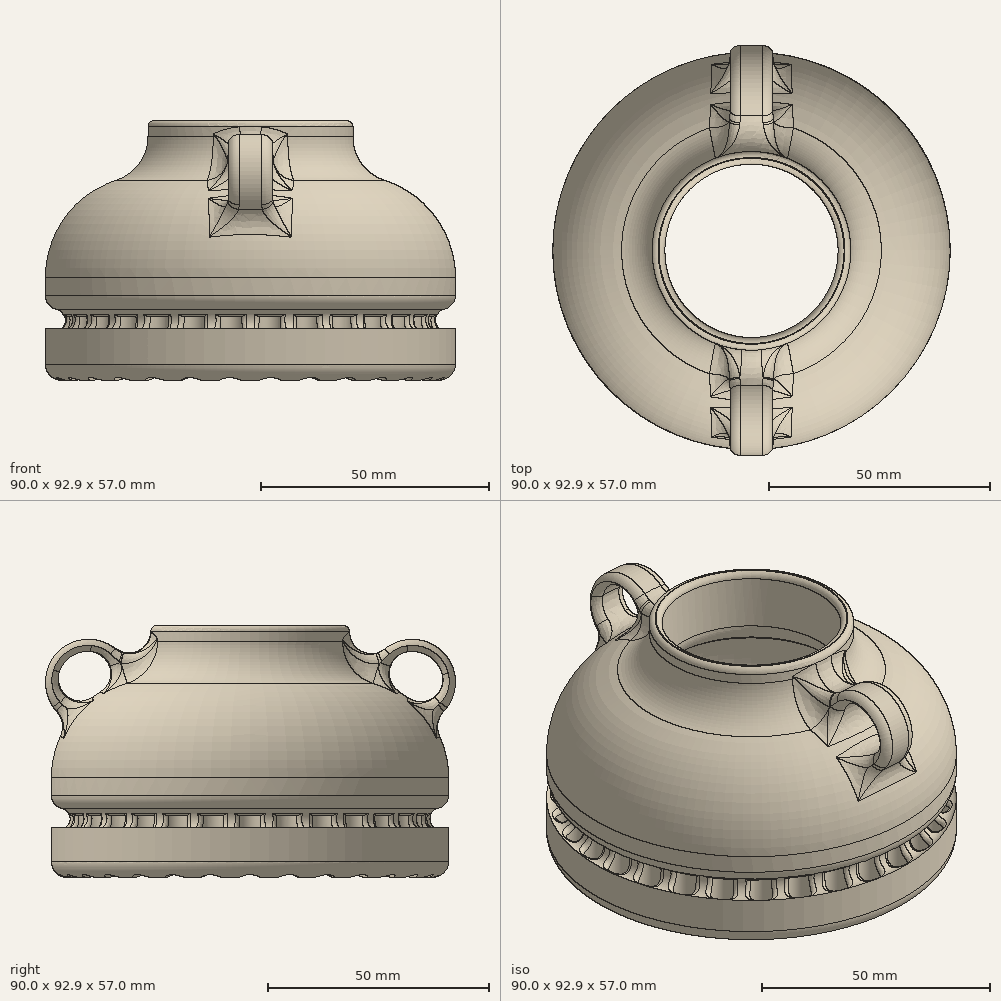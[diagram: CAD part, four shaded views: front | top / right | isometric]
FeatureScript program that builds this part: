
annotation { "Feature Type Name" : "Feature", "Feature Type Description" : "" }
export const myFeature = defineFeature(function(context is Context, id is Id, definition is map)
    precondition{}
    {
        {
            var Q0;
            Q0=qCreatedBy(makeId("Top.planeOp"),FACE);
            var sketch = newSketch(context, id + "F0", { "sketchPlane" : qUnion([Q0])});
            skCircle(sketch, "E0", {"center": v(0, 0) * mm, "radius": 45 * mm});
            skSolve(sketch);
        }
        {
            var Q0;
            Q0 = qSketchRegion(id + "F0", true);
            extrude(context, id + "F1", {"entities" : qUnion([Q0]), "depth" : 45 * mm});
        }
        {
            var Q0;
            Q0=makeQuery(id+"F1.opExtrude","CAP_EDGE",EDGE,{"disambiguationData":[OSD([sQuery(id+"F0.wireOp",EDGE,"E0")])],"isStart":false});
            fillet(context, id + "F2", {"entities" : qUnion([Q0]), "radius" : 22.5 * mm, "tangentPropagation" : true, "allowEdgeOverflow" : false});
        }
        {
            var Q0;
            Q0=makeQuery(id+"F1.opExtrude","CAP_FACE",FACE,{"disambiguationData":[OSD([sQuery(id+"F0.wireOp",EDGE,"E0")])],"isStart":false});
            var sketch = newSketch(context, id + "F3", { "sketchPlane" : qUnion([Q0])});
            skCircle(sketch, "E1", {"center": v(0, 0) * mm, "radius": 22.5 * mm});
            skSolve(sketch);
        }
        {
            var Q0;
            Q0 = qSketchRegion(id + "F3", true);
            extrude(context, id + "F4", {"entities" : qUnion([Q0]), "operationType" : NewBodyOperationType.ADD, "depth" : 12 * mm});
        }
        {
            var Q0;
            Q0=qCreatedBy(makeId("Top.planeOp"),FACE);
            var sketch = newSketch(context, id + "F5", { "sketchPlane" : qUnion([Q0])});
            skCircle(sketch, "E2", {"center": v(0, 0) * mm, "radius": 19.62 * mm});
            skSolve(sketch);
        }
        {
            var Q0;
            {var subQ0=sQuery(id+"F0.wireOp",EDGE,"E0");Q0=makeQuery(id+"F4.boolean.opBoolean","MERGE",EDGE,{"derivedFrom":[makeQuery(id+"F2.opFillet","BLEND_EDGE",EDGE,{"blendedFrom":[makeQuery(id+"F1.opExtrude","CAP_EDGE",EDGE,{"disambiguationData":[OSD([subQ0])],"isStart":false}),makeQuery(id+"F1.opExtrude","CAP_FACE",FACE,{"disambiguationData":[OSD([subQ0])],"isStart":false})],"blendedInto":[makeQuery(id+"F1.opExtrude","CAP_FACE",FACE,{"disambiguationData":[OSD([subQ0])],"isStart":false})]}),makeQuery(id+"F4.opExtrude","CAP_EDGE",EDGE,{"disambiguationData":[OSD([sQuery(id+"F3.wireOp",EDGE,"E1")])],"isStart":true})]});}
            fillet(context, id + "F6", {"entities" : qUnion([Q0]), "radius" : 10 * mm, "tangentPropagation" : true, "allowEdgeOverflow" : false});
        }
        {
            var Q0;
            Q0=makeQuery(id+"F1.opExtrude","CAP_FACE",FACE,{"disambiguationData":[OSD([sQuery(id+"F0.wireOp",EDGE,"E0")])],"isStart":true});
            shell(context, id + "F7", {"entities" : qUnion([Q0]), "thickness" : 7.5 * mm});
        }
        {
            var Q0;
            Q0 = qSketchRegion(id + "F5", true);
            extrude(context, id + "F8", {"entities" : qUnion([Q0]), "operationType" : NewBodyOperationType.REMOVE, "depth" : 80 * mm});
        }
        {
            var Q0;
            Q0=makeQuery(id+"F8.boolean.opBoolean","INTERSECT",EDGE,{"derivedFrom":[makeQuery(id+"F7.opShell","OFFSET_FACE",FACE,{"disambiguationData":[OSD([sQuery(id+"F0.wireOp",EDGE,"E0"),sQuery(id+"F3.wireOp",EDGE,"E1")])]}),makeQuery(id+"F8.opExtrude","SWEPT_FACE",FACE,{"disambiguationData":[OSD([sQuery(id+"F5.wireOp",EDGE,"E2")])]})]});
            fillet(context, id + "F9", {"entities" : qUnion([Q0]), "radius" : 5 * mm, "tangentPropagation" : true, "allowEdgeOverflow" : false});
        }
        {
            var Q0;
            Q0=makeQuery(id+"F1.opExtrude","CAP_FACE",FACE,{"disambiguationData":[OSD([sQuery(id+"F0.wireOp",EDGE,"E0")])],"isStart":true});
            var sketch = newSketch(context, id + "F10", { "sketchPlane" : qUnion([Q0])});
            skCircle(sketch, "E3", {"center": v(-40.97, 0) * mm, "radius": 2.5 * mm});
            skPoint(sketch, "E4", {"position": v(0, 0) * mm});
            skCircle(sketch, "E5.1.0", {"center": v(-40.07, -8.52) * mm, "radius": 2.5 * mm});
            skCircle(sketch, "E5.2.0", {"center": v(-37.42, -16.66) * mm, "radius": 2.5 * mm});
            skCircle(sketch, "E5.3.0", {"center": v(-33.14, -24.08) * mm, "radius": 2.5 * mm});
            skCircle(sketch, "E5.4.0", {"center": v(-27.41, -30.44) * mm, "radius": 2.5 * mm});
            skCircle(sketch, "E5.5.0", {"center": v(-20.48, -35.48) * mm, "radius": 2.5 * mm});
            skCircle(sketch, "E5.6.0", {"center": v(-12.66, -38.96) * mm, "radius": 2.5 * mm});
            skCircle(sketch, "E5.7.0", {"center": v(-4.28, -40.74) * mm, "radius": 2.5 * mm});
            skCircle(sketch, "E5.8.0", {"center": v(4.28, -40.74) * mm, "radius": 2.5 * mm});
            skCircle(sketch, "E5.9.0", {"center": v(12.66, -38.96) * mm, "radius": 2.5 * mm});
            skCircle(sketch, "E5.10.0", {"center": v(20.48, -35.48) * mm, "radius": 2.5 * mm});
            skCircle(sketch, "E5.11.0", {"center": v(27.41, -30.44) * mm, "radius": 2.5 * mm});
            skCircle(sketch, "E5.12.0", {"center": v(33.14, -24.08) * mm, "radius": 2.5 * mm});
            skCircle(sketch, "E5.13.0", {"center": v(37.42, -16.66) * mm, "radius": 2.5 * mm});
            skCircle(sketch, "E5.14.0", {"center": v(40.07, -8.52) * mm, "radius": 2.5 * mm});
            skCircle(sketch, "E5.15.0", {"center": v(40.97, 0) * mm, "radius": 2.5 * mm});
            skCircle(sketch, "E5.16.0", {"center": v(40.07, 8.52) * mm, "radius": 2.5 * mm});
            skCircle(sketch, "E5.17.0", {"center": v(37.42, 16.66) * mm, "radius": 2.5 * mm});
            skCircle(sketch, "E5.18.0", {"center": v(33.14, 24.08) * mm, "radius": 2.5 * mm});
            skCircle(sketch, "E5.19.0", {"center": v(27.41, 30.44) * mm, "radius": 2.5 * mm});
            skCircle(sketch, "E5.20.0", {"center": v(20.48, 35.48) * mm, "radius": 2.5 * mm});
            skCircle(sketch, "E5.21.0", {"center": v(12.66, 38.96) * mm, "radius": 2.5 * mm});
            skCircle(sketch, "E5.22.0", {"center": v(4.28, 40.74) * mm, "radius": 2.5 * mm});
            skCircle(sketch, "E5.23.0", {"center": v(-4.28, 40.74) * mm, "radius": 2.5 * mm});
            skCircle(sketch, "E5.24.0", {"center": v(-12.66, 38.96) * mm, "radius": 2.5 * mm});
            skCircle(sketch, "E5.25.0", {"center": v(-20.48, 35.48) * mm, "radius": 2.5 * mm});
            skCircle(sketch, "E5.26.0", {"center": v(-27.41, 30.44) * mm, "radius": 2.5 * mm});
            skCircle(sketch, "E5.27.0", {"center": v(-33.14, 24.08) * mm, "radius": 2.5 * mm});
            skCircle(sketch, "E5.28.0", {"center": v(-37.42, 16.66) * mm, "radius": 2.5 * mm});
            skCircle(sketch, "E5.29.0", {"center": v(-40.07, 8.52) * mm, "radius": 2.5 * mm});
            skSolve(sketch);
        }
        {
            var Q0;
            Q0 = qSketchRegion(id + "F10", true);
            extrude(context, id + "F11", {"entities" : qUnion([Q0]), "operationType" : NewBodyOperationType.REMOVE, "oppositeDirection" : true, "depth" : 14 * mm});
        }
        {
            var Q0;
            Q0=qCreatedBy(makeId("Front.planeOp"),FACE);
            var sketch = newSketch(context, id + "F12", { "sketchPlane" : qUnion([Q0])});
            skCircle(sketch, "E6", {"center": v(-43.26, 13.19) * mm, "radius": 2.5 * mm});
            skLineSegment(sketch, "E7", {"start": v(0, 0) * mm, "end": v(0, 30.84) * mm});
            skSolve(sketch);
        }
        {
            var Q0;
            Q0=makeQuery(id+"F12.imprint","IMPRINT",FACE,{"disambiguationData":[TD([[makeQuery(id+"F12.imprint","IMPRINT",EDGE,{"derivedFrom":sQuery(id+"F12.wireOp",EDGE,"E6")}),1.0]])]});
            var Q1;
            Q1=sQuery(id+"F12.wireOp",EDGE,"E7");
            revolve(context, id + "F13", {"operationType" : NewBodyOperationType.REMOVE, "entities" : qUnion([Q0]), "axis" : qUnion([Q1]), "revolveType" : RevolveType.FULL, "oppositeDirection" : true});
        }
        {
            var Q0;
            Q0=makeQuery(id+"F13.boolean.opBoolean","INTERSECT",EDGE,{"disambiguationData":[OD(1.0)],"derivedFrom":[makeQuery(id+"F1.opExtrude","SWEPT_FACE",FACE,{"disambiguationData":[OSD([sQuery(id+"F0.wireOp",EDGE,"E0")])]}),makeQuery(id+"F13.opRevolve","SWEPT_FACE",FACE,{"disambiguationData":[OSD([sQuery(id+"F12.wireOp",EDGE,"E6")])]})]});
            fillet(context, id + "F14", {"entities" : qUnion([Q0]), "radius" : 3 * mm, "tangentPropagation" : true, "allowEdgeOverflow" : false});
        }
        {
            var Q0;
            Q0=makeQuery(id+"F4.opExtrude","CAP_EDGE",EDGE,{"disambiguationData":[OSD([sQuery(id+"F3.wireOp",EDGE,"E1")])],"isStart":false});
            var Q1;
            Q1=makeQuery(id+"F8.boolean.opBoolean","INTERSECT",EDGE,{"derivedFrom":[makeQuery(id+"F4.opExtrude","CAP_FACE",FACE,{"disambiguationData":[OSD([sQuery(id+"F3.wireOp",EDGE,"E1")])],"isStart":false}),makeQuery(id+"F8.opExtrude","SWEPT_FACE",FACE,{"disambiguationData":[OSD([sQuery(id+"F5.wireOp",EDGE,"E2")])]})]});
            fillet(context, id + "F15", {"entities" : qUnion([Q0, Q1]), "radius" : 1.35 * mm, "tangentPropagation" : true, "allowEdgeOverflow" : false});
        }
        {
            var Q0;
            Q0=makeQuery(id+"F1.opExtrude","CAP_EDGE",EDGE,{"disambiguationData":[OSD([sQuery(id+"F0.wireOp",EDGE,"E0")])],"isStart":true});
            var Q1;
            {var subQ0=sQuery(id+"F0.wireOp",EDGE,"E0");Q1=makeQuery(id+"F7.opShell","OFFSET_EDGE",EDGE,{"disambiguationData":[OSD([subQ0]),TDD([makeQuery(id+"F1.opExtrude","CAP_EDGE",EDGE,{"disambiguationData":[OSD([subQ0])],"isStart":true})])]});}
            fillet(context, id + "F16", {"entities" : qUnion([Q0, Q1]), "radius" : 3.5 * mm, "tangentPropagation" : true, "allowEdgeOverflow" : false});
        }
        {
            var Q0;
            Q0=makeQuery(id+"F13.boolean.opBoolean","INTERSECT",EDGE,{"derivedFrom":[makeQuery(id+"F11.boolean.opBoolean","COPY",FACE,{"derivedFrom":makeQuery(id+"F11.opExtrude","SWEPT_FACE",FACE,{"disambiguationData":[OSD([sQuery(id+"F10.wireOp",EDGE,"E5.25.0")])]})}),makeQuery(id+"F13.opRevolve","SWEPT_FACE",FACE,{"disambiguationData":[OSD([sQuery(id+"F12.wireOp",EDGE,"E6")])]})]});
            var Q1;
            Q1=makeQuery(id+"F13.boolean.opBoolean","INTERSECT",EDGE,{"derivedFrom":[makeQuery(id+"F11.boolean.opBoolean","COPY",FACE,{"derivedFrom":makeQuery(id+"F11.opExtrude","CAP_FACE",FACE,{"disambiguationData":[OSD([sQuery(id+"F10.wireOp",EDGE,"E5.25.0")])],"isStart":false})}),makeQuery(id+"F13.opRevolve","SWEPT_FACE",FACE,{"disambiguationData":[OSD([sQuery(id+"F12.wireOp",EDGE,"E6")])]})]});
            var Q2;
            Q2=makeQuery(id+"F13.boolean.opBoolean","INTERSECT",EDGE,{"derivedFrom":[makeQuery(id+"F11.boolean.opBoolean","COPY",FACE,{"derivedFrom":makeQuery(id+"F11.opExtrude","SWEPT_FACE",FACE,{"disambiguationData":[OSD([sQuery(id+"F10.wireOp",EDGE,"E5.26.0")])]})}),makeQuery(id+"F13.opRevolve","SWEPT_FACE",FACE,{"disambiguationData":[OSD([sQuery(id+"F12.wireOp",EDGE,"E6")])]})]});
            var Q3;
            Q3=makeQuery(id+"F13.boolean.opBoolean","INTERSECT",EDGE,{"derivedFrom":[makeQuery(id+"F11.boolean.opBoolean","COPY",FACE,{"derivedFrom":makeQuery(id+"F11.opExtrude","CAP_FACE",FACE,{"disambiguationData":[OSD([sQuery(id+"F10.wireOp",EDGE,"E5.26.0")])],"isStart":false})}),makeQuery(id+"F13.opRevolve","SWEPT_FACE",FACE,{"disambiguationData":[OSD([sQuery(id+"F12.wireOp",EDGE,"E6")])]})]});
            var Q4;
            Q4=makeQuery(id+"F13.boolean.opBoolean","INTERSECT",EDGE,{"derivedFrom":[makeQuery(id+"F11.boolean.opBoolean","COPY",FACE,{"derivedFrom":makeQuery(id+"F11.opExtrude","SWEPT_FACE",FACE,{"disambiguationData":[OSD([sQuery(id+"F10.wireOp",EDGE,"E5.27.0")])]})}),makeQuery(id+"F13.opRevolve","SWEPT_FACE",FACE,{"disambiguationData":[OSD([sQuery(id+"F12.wireOp",EDGE,"E6")])]})]});
            var Q5;
            Q5=makeQuery(id+"F13.boolean.opBoolean","INTERSECT",EDGE,{"derivedFrom":[makeQuery(id+"F11.boolean.opBoolean","COPY",FACE,{"derivedFrom":makeQuery(id+"F11.opExtrude","CAP_FACE",FACE,{"disambiguationData":[OSD([sQuery(id+"F10.wireOp",EDGE,"E5.27.0")])],"isStart":false})}),makeQuery(id+"F13.opRevolve","SWEPT_FACE",FACE,{"disambiguationData":[OSD([sQuery(id+"F12.wireOp",EDGE,"E6")])]})]});
            var Q6;
            Q6=makeQuery(id+"F13.boolean.opBoolean","INTERSECT",EDGE,{"derivedFrom":[makeQuery(id+"F11.boolean.opBoolean","COPY",FACE,{"derivedFrom":makeQuery(id+"F11.opExtrude","SWEPT_FACE",FACE,{"disambiguationData":[OSD([sQuery(id+"F10.wireOp",EDGE,"E5.28.0")])]})}),makeQuery(id+"F13.opRevolve","SWEPT_FACE",FACE,{"disambiguationData":[OSD([sQuery(id+"F12.wireOp",EDGE,"E6")])]})]});
            var Q7;
            Q7=makeQuery(id+"F13.boolean.opBoolean","INTERSECT",EDGE,{"derivedFrom":[makeQuery(id+"F11.boolean.opBoolean","COPY",FACE,{"derivedFrom":makeQuery(id+"F11.opExtrude","CAP_FACE",FACE,{"disambiguationData":[OSD([sQuery(id+"F10.wireOp",EDGE,"E5.28.0")])],"isStart":false})}),makeQuery(id+"F13.opRevolve","SWEPT_FACE",FACE,{"disambiguationData":[OSD([sQuery(id+"F12.wireOp",EDGE,"E6")])]})]});
            var Q8;
            Q8=makeQuery(id+"F13.boolean.opBoolean","INTERSECT",EDGE,{"derivedFrom":[makeQuery(id+"F11.boolean.opBoolean","COPY",FACE,{"derivedFrom":makeQuery(id+"F11.opExtrude","SWEPT_FACE",FACE,{"disambiguationData":[OSD([sQuery(id+"F10.wireOp",EDGE,"E5.24.0")])]})}),makeQuery(id+"F13.opRevolve","SWEPT_FACE",FACE,{"disambiguationData":[OSD([sQuery(id+"F12.wireOp",EDGE,"E6")])]})]});
            var Q9;
            Q9=makeQuery(id+"F13.boolean.opBoolean","INTERSECT",EDGE,{"derivedFrom":[makeQuery(id+"F11.boolean.opBoolean","COPY",FACE,{"derivedFrom":makeQuery(id+"F11.opExtrude","CAP_FACE",FACE,{"disambiguationData":[OSD([sQuery(id+"F10.wireOp",EDGE,"E5.24.0")])],"isStart":false})}),makeQuery(id+"F13.opRevolve","SWEPT_FACE",FACE,{"disambiguationData":[OSD([sQuery(id+"F12.wireOp",EDGE,"E6")])]})]});
            var Q10;
            Q10=makeQuery(id+"F13.boolean.opBoolean","INTERSECT",EDGE,{"derivedFrom":[makeQuery(id+"F11.boolean.opBoolean","COPY",FACE,{"derivedFrom":makeQuery(id+"F11.opExtrude","SWEPT_FACE",FACE,{"disambiguationData":[OSD([sQuery(id+"F10.wireOp",EDGE,"E5.29.0")])]})}),makeQuery(id+"F13.opRevolve","SWEPT_FACE",FACE,{"disambiguationData":[OSD([sQuery(id+"F12.wireOp",EDGE,"E6")])]})]});
            var Q11;
            Q11=makeQuery(id+"F13.boolean.opBoolean","INTERSECT",EDGE,{"derivedFrom":[makeQuery(id+"F11.boolean.opBoolean","COPY",FACE,{"derivedFrom":makeQuery(id+"F11.opExtrude","CAP_FACE",FACE,{"disambiguationData":[OSD([sQuery(id+"F10.wireOp",EDGE,"E5.29.0")])],"isStart":false})}),makeQuery(id+"F13.opRevolve","SWEPT_FACE",FACE,{"disambiguationData":[OSD([sQuery(id+"F12.wireOp",EDGE,"E6")])]})]});
            var Q12;
            Q12=makeQuery(id+"F13.boolean.opBoolean","INTERSECT",EDGE,{"derivedFrom":[makeQuery(id+"F11.boolean.opBoolean","COPY",FACE,{"derivedFrom":makeQuery(id+"F11.opExtrude","CAP_FACE",FACE,{"disambiguationData":[OSD([sQuery(id+"F10.wireOp",EDGE,"E5.8.0")])],"isStart":false})}),makeQuery(id+"F13.opRevolve","SWEPT_FACE",FACE,{"disambiguationData":[OSD([sQuery(id+"F12.wireOp",EDGE,"E6")])]})]});
            var Q13;
            Q13=makeQuery(id+"F13.boolean.opBoolean","INTERSECT",EDGE,{"derivedFrom":[makeQuery(id+"F11.boolean.opBoolean","COPY",FACE,{"derivedFrom":makeQuery(id+"F11.opExtrude","SWEPT_FACE",FACE,{"disambiguationData":[OSD([sQuery(id+"F10.wireOp",EDGE,"E5.8.0")])]})}),makeQuery(id+"F13.opRevolve","SWEPT_FACE",FACE,{"disambiguationData":[OSD([sQuery(id+"F12.wireOp",EDGE,"E6")])]})]});
            var Q14;
            Q14=makeQuery(id+"F13.boolean.opBoolean","INTERSECT",EDGE,{"derivedFrom":[makeQuery(id+"F11.boolean.opBoolean","COPY",FACE,{"derivedFrom":makeQuery(id+"F11.opExtrude","CAP_FACE",FACE,{"disambiguationData":[OSD([sQuery(id+"F10.wireOp",EDGE,"E5.9.0")])],"isStart":false})}),makeQuery(id+"F13.opRevolve","SWEPT_FACE",FACE,{"disambiguationData":[OSD([sQuery(id+"F12.wireOp",EDGE,"E6")])]})]});
            var Q15;
            Q15=makeQuery(id+"F13.boolean.opBoolean","INTERSECT",EDGE,{"derivedFrom":[makeQuery(id+"F11.boolean.opBoolean","COPY",FACE,{"derivedFrom":makeQuery(id+"F11.opExtrude","SWEPT_FACE",FACE,{"disambiguationData":[OSD([sQuery(id+"F10.wireOp",EDGE,"E5.9.0")])]})}),makeQuery(id+"F13.opRevolve","SWEPT_FACE",FACE,{"disambiguationData":[OSD([sQuery(id+"F12.wireOp",EDGE,"E6")])]})]});
            var Q16;
            Q16=makeQuery(id+"F13.boolean.opBoolean","INTERSECT",EDGE,{"derivedFrom":[makeQuery(id+"F11.boolean.opBoolean","COPY",FACE,{"derivedFrom":makeQuery(id+"F11.opExtrude","CAP_FACE",FACE,{"disambiguationData":[OSD([sQuery(id+"F10.wireOp",EDGE,"E5.10.0")])],"isStart":false})}),makeQuery(id+"F13.opRevolve","SWEPT_FACE",FACE,{"disambiguationData":[OSD([sQuery(id+"F12.wireOp",EDGE,"E6")])]})]});
            var Q17;
            Q17=makeQuery(id+"F13.boolean.opBoolean","INTERSECT",EDGE,{"derivedFrom":[makeQuery(id+"F11.boolean.opBoolean","COPY",FACE,{"derivedFrom":makeQuery(id+"F11.opExtrude","SWEPT_FACE",FACE,{"disambiguationData":[OSD([sQuery(id+"F10.wireOp",EDGE,"E5.10.0")])]})}),makeQuery(id+"F13.opRevolve","SWEPT_FACE",FACE,{"disambiguationData":[OSD([sQuery(id+"F12.wireOp",EDGE,"E6")])]})]});
            var Q18;
            Q18=makeQuery(id+"F13.boolean.opBoolean","INTERSECT",EDGE,{"derivedFrom":[makeQuery(id+"F11.boolean.opBoolean","COPY",FACE,{"derivedFrom":makeQuery(id+"F11.opExtrude","CAP_FACE",FACE,{"disambiguationData":[OSD([sQuery(id+"F10.wireOp",EDGE,"E5.11.0")])],"isStart":false})}),makeQuery(id+"F13.opRevolve","SWEPT_FACE",FACE,{"disambiguationData":[OSD([sQuery(id+"F12.wireOp",EDGE,"E6")])]})]});
            var Q19;
            Q19=makeQuery(id+"F13.boolean.opBoolean","INTERSECT",EDGE,{"derivedFrom":[makeQuery(id+"F11.boolean.opBoolean","COPY",FACE,{"derivedFrom":makeQuery(id+"F11.opExtrude","SWEPT_FACE",FACE,{"disambiguationData":[OSD([sQuery(id+"F10.wireOp",EDGE,"E5.11.0")])]})}),makeQuery(id+"F13.opRevolve","SWEPT_FACE",FACE,{"disambiguationData":[OSD([sQuery(id+"F12.wireOp",EDGE,"E6")])]})]});
            var Q20;
            Q20=makeQuery(id+"F13.boolean.opBoolean","INTERSECT",EDGE,{"derivedFrom":[makeQuery(id+"F11.boolean.opBoolean","COPY",FACE,{"derivedFrom":makeQuery(id+"F11.opExtrude","CAP_FACE",FACE,{"disambiguationData":[OSD([sQuery(id+"F10.wireOp",EDGE,"E5.12.0")])],"isStart":false})}),makeQuery(id+"F13.opRevolve","SWEPT_FACE",FACE,{"disambiguationData":[OSD([sQuery(id+"F12.wireOp",EDGE,"E6")])]})]});
            var Q21;
            Q21=makeQuery(id+"F13.boolean.opBoolean","INTERSECT",EDGE,{"derivedFrom":[makeQuery(id+"F11.boolean.opBoolean","COPY",FACE,{"derivedFrom":makeQuery(id+"F11.opExtrude","SWEPT_FACE",FACE,{"disambiguationData":[OSD([sQuery(id+"F10.wireOp",EDGE,"E5.12.0")])]})}),makeQuery(id+"F13.opRevolve","SWEPT_FACE",FACE,{"disambiguationData":[OSD([sQuery(id+"F12.wireOp",EDGE,"E6")])]})]});
            var Q22;
            Q22=makeQuery(id+"F13.boolean.opBoolean","INTERSECT",EDGE,{"derivedFrom":[makeQuery(id+"F11.boolean.opBoolean","COPY",FACE,{"derivedFrom":makeQuery(id+"F11.opExtrude","SWEPT_FACE",FACE,{"disambiguationData":[OSD([sQuery(id+"F10.wireOp",EDGE,"E5.13.0")])]})}),makeQuery(id+"F13.opRevolve","SWEPT_FACE",FACE,{"disambiguationData":[OSD([sQuery(id+"F12.wireOp",EDGE,"E6")])]})]});
            var Q23;
            Q23=makeQuery(id+"F13.boolean.opBoolean","INTERSECT",EDGE,{"derivedFrom":[makeQuery(id+"F11.boolean.opBoolean","COPY",FACE,{"derivedFrom":makeQuery(id+"F11.opExtrude","CAP_FACE",FACE,{"disambiguationData":[OSD([sQuery(id+"F10.wireOp",EDGE,"E5.13.0")])],"isStart":false})}),makeQuery(id+"F13.opRevolve","SWEPT_FACE",FACE,{"disambiguationData":[OSD([sQuery(id+"F12.wireOp",EDGE,"E6")])]})]});
            var Q24;
            Q24=makeQuery(id+"F13.boolean.opBoolean","INTERSECT",EDGE,{"derivedFrom":[makeQuery(id+"F11.boolean.opBoolean","COPY",FACE,{"derivedFrom":makeQuery(id+"F11.opExtrude","SWEPT_FACE",FACE,{"disambiguationData":[OSD([sQuery(id+"F10.wireOp",EDGE,"E5.14.0")])]})}),makeQuery(id+"F13.opRevolve","SWEPT_FACE",FACE,{"disambiguationData":[OSD([sQuery(id+"F12.wireOp",EDGE,"E6")])]})]});
            var Q25;
            Q25=makeQuery(id+"F13.boolean.opBoolean","INTERSECT",EDGE,{"derivedFrom":[makeQuery(id+"F11.boolean.opBoolean","COPY",FACE,{"derivedFrom":makeQuery(id+"F11.opExtrude","CAP_FACE",FACE,{"disambiguationData":[OSD([sQuery(id+"F10.wireOp",EDGE,"E5.14.0")])],"isStart":false})}),makeQuery(id+"F13.opRevolve","SWEPT_FACE",FACE,{"disambiguationData":[OSD([sQuery(id+"F12.wireOp",EDGE,"E6")])]})]});
            var Q26;
            Q26=makeQuery(id+"F13.boolean.opBoolean","INTERSECT",EDGE,{"derivedFrom":[makeQuery(id+"F11.boolean.opBoolean","COPY",FACE,{"derivedFrom":makeQuery(id+"F11.opExtrude","CAP_FACE",FACE,{"disambiguationData":[OSD([sQuery(id+"F10.wireOp",EDGE,"E5.7.0")])],"isStart":false})}),makeQuery(id+"F13.opRevolve","SWEPT_FACE",FACE,{"disambiguationData":[OSD([sQuery(id+"F12.wireOp",EDGE,"E6")])]})]});
            var Q27;
            Q27=makeQuery(id+"F13.boolean.opBoolean","INTERSECT",EDGE,{"derivedFrom":[makeQuery(id+"F11.boolean.opBoolean","COPY",FACE,{"derivedFrom":makeQuery(id+"F11.opExtrude","SWEPT_FACE",FACE,{"disambiguationData":[OSD([sQuery(id+"F10.wireOp",EDGE,"E5.7.0")])]})}),makeQuery(id+"F13.opRevolve","SWEPT_FACE",FACE,{"disambiguationData":[OSD([sQuery(id+"F12.wireOp",EDGE,"E6")])]})]});
            var Q28;
            Q28=makeQuery(id+"F13.boolean.opBoolean","INTERSECT",EDGE,{"derivedFrom":[makeQuery(id+"F11.boolean.opBoolean","COPY",FACE,{"derivedFrom":makeQuery(id+"F11.opExtrude","CAP_FACE",FACE,{"disambiguationData":[OSD([sQuery(id+"F10.wireOp",EDGE,"E5.6.0")])],"isStart":false})}),makeQuery(id+"F13.opRevolve","SWEPT_FACE",FACE,{"disambiguationData":[OSD([sQuery(id+"F12.wireOp",EDGE,"E6")])]})]});
            var Q29;
            Q29=makeQuery(id+"F13.boolean.opBoolean","INTERSECT",EDGE,{"derivedFrom":[makeQuery(id+"F11.boolean.opBoolean","COPY",FACE,{"derivedFrom":makeQuery(id+"F11.opExtrude","SWEPT_FACE",FACE,{"disambiguationData":[OSD([sQuery(id+"F10.wireOp",EDGE,"E5.6.0")])]})}),makeQuery(id+"F13.opRevolve","SWEPT_FACE",FACE,{"disambiguationData":[OSD([sQuery(id+"F12.wireOp",EDGE,"E6")])]})]});
            var Q30;
            Q30=makeQuery(id+"F13.boolean.opBoolean","INTERSECT",EDGE,{"derivedFrom":[makeQuery(id+"F11.boolean.opBoolean","COPY",FACE,{"derivedFrom":makeQuery(id+"F11.opExtrude","CAP_FACE",FACE,{"disambiguationData":[OSD([sQuery(id+"F10.wireOp",EDGE,"E5.5.0")])],"isStart":false})}),makeQuery(id+"F13.opRevolve","SWEPT_FACE",FACE,{"disambiguationData":[OSD([sQuery(id+"F12.wireOp",EDGE,"E6")])]})]});
            var Q31;
            Q31=makeQuery(id+"F13.boolean.opBoolean","INTERSECT",EDGE,{"derivedFrom":[makeQuery(id+"F11.boolean.opBoolean","COPY",FACE,{"derivedFrom":makeQuery(id+"F11.opExtrude","SWEPT_FACE",FACE,{"disambiguationData":[OSD([sQuery(id+"F10.wireOp",EDGE,"E5.5.0")])]})}),makeQuery(id+"F13.opRevolve","SWEPT_FACE",FACE,{"disambiguationData":[OSD([sQuery(id+"F12.wireOp",EDGE,"E6")])]})]});
            var Q32;
            Q32=makeQuery(id+"F13.boolean.opBoolean","INTERSECT",EDGE,{"derivedFrom":[makeQuery(id+"F11.boolean.opBoolean","COPY",FACE,{"derivedFrom":makeQuery(id+"F11.opExtrude","CAP_FACE",FACE,{"disambiguationData":[OSD([sQuery(id+"F10.wireOp",EDGE,"E5.4.0")])],"isStart":false})}),makeQuery(id+"F13.opRevolve","SWEPT_FACE",FACE,{"disambiguationData":[OSD([sQuery(id+"F12.wireOp",EDGE,"E6")])]})]});
            var Q33;
            Q33=makeQuery(id+"F13.boolean.opBoolean","INTERSECT",EDGE,{"derivedFrom":[makeQuery(id+"F11.boolean.opBoolean","COPY",FACE,{"derivedFrom":makeQuery(id+"F11.opExtrude","SWEPT_FACE",FACE,{"disambiguationData":[OSD([sQuery(id+"F10.wireOp",EDGE,"E5.4.0")])]})}),makeQuery(id+"F13.opRevolve","SWEPT_FACE",FACE,{"disambiguationData":[OSD([sQuery(id+"F12.wireOp",EDGE,"E6")])]})]});
            var Q34;
            Q34=makeQuery(id+"F13.boolean.opBoolean","INTERSECT",EDGE,{"derivedFrom":[makeQuery(id+"F11.boolean.opBoolean","COPY",FACE,{"derivedFrom":makeQuery(id+"F11.opExtrude","CAP_FACE",FACE,{"disambiguationData":[OSD([sQuery(id+"F10.wireOp",EDGE,"E5.3.0")])],"isStart":false})}),makeQuery(id+"F13.opRevolve","SWEPT_FACE",FACE,{"disambiguationData":[OSD([sQuery(id+"F12.wireOp",EDGE,"E6")])]})]});
            var Q35;
            Q35=makeQuery(id+"F13.boolean.opBoolean","INTERSECT",EDGE,{"derivedFrom":[makeQuery(id+"F11.boolean.opBoolean","COPY",FACE,{"derivedFrom":makeQuery(id+"F11.opExtrude","SWEPT_FACE",FACE,{"disambiguationData":[OSD([sQuery(id+"F10.wireOp",EDGE,"E5.3.0")])]})}),makeQuery(id+"F13.opRevolve","SWEPT_FACE",FACE,{"disambiguationData":[OSD([sQuery(id+"F12.wireOp",EDGE,"E6")])]})]});
            var Q36;
            Q36=makeQuery(id+"F13.boolean.opBoolean","INTERSECT",EDGE,{"derivedFrom":[makeQuery(id+"F11.boolean.opBoolean","COPY",FACE,{"derivedFrom":makeQuery(id+"F11.opExtrude","CAP_FACE",FACE,{"disambiguationData":[OSD([sQuery(id+"F10.wireOp",EDGE,"E5.2.0")])],"isStart":false})}),makeQuery(id+"F13.opRevolve","SWEPT_FACE",FACE,{"disambiguationData":[OSD([sQuery(id+"F12.wireOp",EDGE,"E6")])]})]});
            var Q37;
            Q37=makeQuery(id+"F13.boolean.opBoolean","INTERSECT",EDGE,{"derivedFrom":[makeQuery(id+"F11.boolean.opBoolean","COPY",FACE,{"derivedFrom":makeQuery(id+"F11.opExtrude","SWEPT_FACE",FACE,{"disambiguationData":[OSD([sQuery(id+"F10.wireOp",EDGE,"E5.2.0")])]})}),makeQuery(id+"F13.opRevolve","SWEPT_FACE",FACE,{"disambiguationData":[OSD([sQuery(id+"F12.wireOp",EDGE,"E6")])]})]});
            var Q38;
            Q38=makeQuery(id+"F13.boolean.opBoolean","INTERSECT",EDGE,{"derivedFrom":[makeQuery(id+"F11.boolean.opBoolean","COPY",FACE,{"derivedFrom":makeQuery(id+"F11.opExtrude","SWEPT_FACE",FACE,{"disambiguationData":[OSD([sQuery(id+"F10.wireOp",EDGE,"E5.1.0")])]})}),makeQuery(id+"F13.opRevolve","SWEPT_FACE",FACE,{"disambiguationData":[OSD([sQuery(id+"F12.wireOp",EDGE,"E6")])]})]});
            var Q39;
            Q39=makeQuery(id+"F13.boolean.opBoolean","INTERSECT",EDGE,{"derivedFrom":[makeQuery(id+"F11.boolean.opBoolean","COPY",FACE,{"derivedFrom":makeQuery(id+"F11.opExtrude","CAP_FACE",FACE,{"disambiguationData":[OSD([sQuery(id+"F10.wireOp",EDGE,"E3")])],"isStart":false})}),makeQuery(id+"F13.opRevolve","SWEPT_FACE",FACE,{"disambiguationData":[OSD([sQuery(id+"F12.wireOp",EDGE,"E6")])]})]});
            var Q40;
            Q40=makeQuery(id+"F13.boolean.opBoolean","INTERSECT",EDGE,{"derivedFrom":[makeQuery(id+"F11.boolean.opBoolean","COPY",FACE,{"derivedFrom":makeQuery(id+"F11.opExtrude","SWEPT_FACE",FACE,{"disambiguationData":[OSD([sQuery(id+"F10.wireOp",EDGE,"E3")])]})}),makeQuery(id+"F13.opRevolve","SWEPT_FACE",FACE,{"disambiguationData":[OSD([sQuery(id+"F12.wireOp",EDGE,"E6")])]})]});
            var Q41;
            Q41=makeQuery(id+"F13.boolean.opBoolean","INTERSECT",EDGE,{"derivedFrom":[makeQuery(id+"F11.boolean.opBoolean","COPY",FACE,{"derivedFrom":makeQuery(id+"F11.opExtrude","CAP_FACE",FACE,{"disambiguationData":[OSD([sQuery(id+"F10.wireOp",EDGE,"E5.1.0")])],"isStart":false})}),makeQuery(id+"F13.opRevolve","SWEPT_FACE",FACE,{"disambiguationData":[OSD([sQuery(id+"F12.wireOp",EDGE,"E6")])]})]});
            var Q42;
            Q42=makeQuery(id+"F13.boolean.opBoolean","INTERSECT",EDGE,{"derivedFrom":[makeQuery(id+"F11.boolean.opBoolean","COPY",FACE,{"derivedFrom":makeQuery(id+"F11.opExtrude","CAP_FACE",FACE,{"disambiguationData":[OSD([sQuery(id+"F10.wireOp",EDGE,"E5.15.0")])],"isStart":false})}),makeQuery(id+"F13.opRevolve","SWEPT_FACE",FACE,{"disambiguationData":[OSD([sQuery(id+"F12.wireOp",EDGE,"E6")])]})]});
            var Q43;
            Q43=makeQuery(id+"F13.boolean.opBoolean","INTERSECT",EDGE,{"derivedFrom":[makeQuery(id+"F11.boolean.opBoolean","COPY",FACE,{"derivedFrom":makeQuery(id+"F11.opExtrude","SWEPT_FACE",FACE,{"disambiguationData":[OSD([sQuery(id+"F10.wireOp",EDGE,"E5.15.0")])]})}),makeQuery(id+"F13.opRevolve","SWEPT_FACE",FACE,{"disambiguationData":[OSD([sQuery(id+"F12.wireOp",EDGE,"E6")])]})]});
            var Q44;
            Q44=makeQuery(id+"F13.boolean.opBoolean","INTERSECT",EDGE,{"derivedFrom":[makeQuery(id+"F11.boolean.opBoolean","COPY",FACE,{"derivedFrom":makeQuery(id+"F11.opExtrude","CAP_FACE",FACE,{"disambiguationData":[OSD([sQuery(id+"F10.wireOp",EDGE,"E5.16.0")])],"isStart":false})}),makeQuery(id+"F13.opRevolve","SWEPT_FACE",FACE,{"disambiguationData":[OSD([sQuery(id+"F12.wireOp",EDGE,"E6")])]})]});
            var Q45;
            Q45=makeQuery(id+"F13.boolean.opBoolean","INTERSECT",EDGE,{"derivedFrom":[makeQuery(id+"F11.boolean.opBoolean","COPY",FACE,{"derivedFrom":makeQuery(id+"F11.opExtrude","SWEPT_FACE",FACE,{"disambiguationData":[OSD([sQuery(id+"F10.wireOp",EDGE,"E5.16.0")])]})}),makeQuery(id+"F13.opRevolve","SWEPT_FACE",FACE,{"disambiguationData":[OSD([sQuery(id+"F12.wireOp",EDGE,"E6")])]})]});
            var Q46;
            Q46=makeQuery(id+"F13.boolean.opBoolean","INTERSECT",EDGE,{"derivedFrom":[makeQuery(id+"F11.boolean.opBoolean","COPY",FACE,{"derivedFrom":makeQuery(id+"F11.opExtrude","SWEPT_FACE",FACE,{"disambiguationData":[OSD([sQuery(id+"F10.wireOp",EDGE,"E5.17.0")])]})}),makeQuery(id+"F13.opRevolve","SWEPT_FACE",FACE,{"disambiguationData":[OSD([sQuery(id+"F12.wireOp",EDGE,"E6")])]})]});
            var Q47;
            Q47=makeQuery(id+"F13.boolean.opBoolean","INTERSECT",EDGE,{"derivedFrom":[makeQuery(id+"F11.boolean.opBoolean","COPY",FACE,{"derivedFrom":makeQuery(id+"F11.opExtrude","CAP_FACE",FACE,{"disambiguationData":[OSD([sQuery(id+"F10.wireOp",EDGE,"E5.18.0")])],"isStart":false})}),makeQuery(id+"F13.opRevolve","SWEPT_FACE",FACE,{"disambiguationData":[OSD([sQuery(id+"F12.wireOp",EDGE,"E6")])]})]});
            var Q48;
            Q48=makeQuery(id+"F13.boolean.opBoolean","INTERSECT",EDGE,{"derivedFrom":[makeQuery(id+"F11.boolean.opBoolean","COPY",FACE,{"derivedFrom":makeQuery(id+"F11.opExtrude","SWEPT_FACE",FACE,{"disambiguationData":[OSD([sQuery(id+"F10.wireOp",EDGE,"E5.18.0")])]})}),makeQuery(id+"F13.opRevolve","SWEPT_FACE",FACE,{"disambiguationData":[OSD([sQuery(id+"F12.wireOp",EDGE,"E6")])]})]});
            var Q49;
            Q49=makeQuery(id+"F13.boolean.opBoolean","INTERSECT",EDGE,{"derivedFrom":[makeQuery(id+"F11.boolean.opBoolean","COPY",FACE,{"derivedFrom":makeQuery(id+"F11.opExtrude","CAP_FACE",FACE,{"disambiguationData":[OSD([sQuery(id+"F10.wireOp",EDGE,"E5.19.0")])],"isStart":false})}),makeQuery(id+"F13.opRevolve","SWEPT_FACE",FACE,{"disambiguationData":[OSD([sQuery(id+"F12.wireOp",EDGE,"E6")])]})]});
            var Q50;
            Q50=makeQuery(id+"F13.boolean.opBoolean","INTERSECT",EDGE,{"derivedFrom":[makeQuery(id+"F11.boolean.opBoolean","COPY",FACE,{"derivedFrom":makeQuery(id+"F11.opExtrude","SWEPT_FACE",FACE,{"disambiguationData":[OSD([sQuery(id+"F10.wireOp",EDGE,"E5.19.0")])]})}),makeQuery(id+"F13.opRevolve","SWEPT_FACE",FACE,{"disambiguationData":[OSD([sQuery(id+"F12.wireOp",EDGE,"E6")])]})]});
            var Q51;
            Q51=makeQuery(id+"F13.boolean.opBoolean","INTERSECT",EDGE,{"derivedFrom":[makeQuery(id+"F11.boolean.opBoolean","COPY",FACE,{"derivedFrom":makeQuery(id+"F11.opExtrude","CAP_FACE",FACE,{"disambiguationData":[OSD([sQuery(id+"F10.wireOp",EDGE,"E5.20.0")])],"isStart":false})}),makeQuery(id+"F13.opRevolve","SWEPT_FACE",FACE,{"disambiguationData":[OSD([sQuery(id+"F12.wireOp",EDGE,"E6")])]})]});
            var Q52;
            Q52=makeQuery(id+"F13.boolean.opBoolean","INTERSECT",EDGE,{"derivedFrom":[makeQuery(id+"F11.boolean.opBoolean","COPY",FACE,{"derivedFrom":makeQuery(id+"F11.opExtrude","SWEPT_FACE",FACE,{"disambiguationData":[OSD([sQuery(id+"F10.wireOp",EDGE,"E5.20.0")])]})}),makeQuery(id+"F13.opRevolve","SWEPT_FACE",FACE,{"disambiguationData":[OSD([sQuery(id+"F12.wireOp",EDGE,"E6")])]})]});
            var Q53;
            Q53=makeQuery(id+"F13.boolean.opBoolean","INTERSECT",EDGE,{"derivedFrom":[makeQuery(id+"F11.boolean.opBoolean","COPY",FACE,{"derivedFrom":makeQuery(id+"F11.opExtrude","CAP_FACE",FACE,{"disambiguationData":[OSD([sQuery(id+"F10.wireOp",EDGE,"E5.17.0")])],"isStart":false})}),makeQuery(id+"F13.opRevolve","SWEPT_FACE",FACE,{"disambiguationData":[OSD([sQuery(id+"F12.wireOp",EDGE,"E6")])]})]});
            var Q54;
            Q54=makeQuery(id+"F13.boolean.opBoolean","INTERSECT",EDGE,{"derivedFrom":[makeQuery(id+"F11.boolean.opBoolean","COPY",FACE,{"derivedFrom":makeQuery(id+"F11.opExtrude","CAP_FACE",FACE,{"disambiguationData":[OSD([sQuery(id+"F10.wireOp",EDGE,"E5.21.0")])],"isStart":false})}),makeQuery(id+"F13.opRevolve","SWEPT_FACE",FACE,{"disambiguationData":[OSD([sQuery(id+"F12.wireOp",EDGE,"E6")])]})]});
            var Q55;
            Q55=makeQuery(id+"F13.boolean.opBoolean","INTERSECT",EDGE,{"derivedFrom":[makeQuery(id+"F11.boolean.opBoolean","COPY",FACE,{"derivedFrom":makeQuery(id+"F11.opExtrude","SWEPT_FACE",FACE,{"disambiguationData":[OSD([sQuery(id+"F10.wireOp",EDGE,"E5.21.0")])]})}),makeQuery(id+"F13.opRevolve","SWEPT_FACE",FACE,{"disambiguationData":[OSD([sQuery(id+"F12.wireOp",EDGE,"E6")])]})]});
            var Q56;
            Q56=makeQuery(id+"F13.boolean.opBoolean","INTERSECT",EDGE,{"derivedFrom":[makeQuery(id+"F11.boolean.opBoolean","COPY",FACE,{"derivedFrom":makeQuery(id+"F11.opExtrude","CAP_FACE",FACE,{"disambiguationData":[OSD([sQuery(id+"F10.wireOp",EDGE,"E5.22.0")])],"isStart":false})}),makeQuery(id+"F13.opRevolve","SWEPT_FACE",FACE,{"disambiguationData":[OSD([sQuery(id+"F12.wireOp",EDGE,"E6")])]})]});
            var Q57;
            Q57=makeQuery(id+"F13.boolean.opBoolean","INTERSECT",EDGE,{"derivedFrom":[makeQuery(id+"F11.boolean.opBoolean","COPY",FACE,{"derivedFrom":makeQuery(id+"F11.opExtrude","SWEPT_FACE",FACE,{"disambiguationData":[OSD([sQuery(id+"F10.wireOp",EDGE,"E5.22.0")])]})}),makeQuery(id+"F13.opRevolve","SWEPT_FACE",FACE,{"disambiguationData":[OSD([sQuery(id+"F12.wireOp",EDGE,"E6")])]})]});
            var Q58;
            Q58=makeQuery(id+"F13.boolean.opBoolean","INTERSECT",EDGE,{"derivedFrom":[makeQuery(id+"F11.boolean.opBoolean","COPY",FACE,{"derivedFrom":makeQuery(id+"F11.opExtrude","CAP_FACE",FACE,{"disambiguationData":[OSD([sQuery(id+"F10.wireOp",EDGE,"E5.23.0")])],"isStart":false})}),makeQuery(id+"F13.opRevolve","SWEPT_FACE",FACE,{"disambiguationData":[OSD([sQuery(id+"F12.wireOp",EDGE,"E6")])]})]});
            var Q59;
            Q59=makeQuery(id+"F13.boolean.opBoolean","INTERSECT",EDGE,{"derivedFrom":[makeQuery(id+"F11.boolean.opBoolean","COPY",FACE,{"derivedFrom":makeQuery(id+"F11.opExtrude","SWEPT_FACE",FACE,{"disambiguationData":[OSD([sQuery(id+"F10.wireOp",EDGE,"E5.23.0")])]})}),makeQuery(id+"F13.opRevolve","SWEPT_FACE",FACE,{"disambiguationData":[OSD([sQuery(id+"F12.wireOp",EDGE,"E6")])]})]});
            fillet(context, id + "F17", {"entities" : qUnion([Q0, Q1, Q2, Q3, Q4, Q5, Q6, Q7, Q8, Q9, Q10, Q11, Q12, Q13, Q14, Q15, Q16, Q17, Q18, Q19, Q20, Q21, Q22, Q23, Q24, Q25, Q26, Q27, Q28, Q29, Q30, Q31, Q32, Q33, Q34, Q35, Q36, Q37, Q38, Q39, Q40, Q41, Q42, Q43, Q44, Q45, Q46, Q47, Q48, Q49, Q50, Q51, Q52, Q53, Q54, Q55, Q56, Q57, Q58, Q59]), "radius" : 1 * mm, "tangentPropagation" : true, "allowEdgeOverflow" : false});
        }
        {
            var Q0;
            Q0=qCreatedBy(makeId("Right.planeOp"),FACE);
            var sketch = newSketch(context, id + "F18", { "sketchPlane" : qUnion([Q0])});
            skCircle(sketch, "E8", {"center": v(36.78, 44.16) * mm, "radius": 7 * mm});
            skCircle(sketch, "E9", {"center": v(36.78, 44.16) * mm, "radius": 9.75 * mm});
            skCircle(sketch, "E10", {"center": v(-36.59, 44.16) * mm, "radius": 7 * mm});
            skCircle(sketch, "E11", {"center": v(-36.59, 44.16) * mm, "radius": 9.75 * mm});
            skSolve(sketch);
        }
        {
            var Q0;
            Q0 = qSketchRegion(id + "F18", true);
            extrude(context, id + "F19", {"entities" : qUnion([Q0]), "operationType" : NewBodyOperationType.ADD, "depth" : 5 * mm});
        }
        {
            var Q0;
            Q0 = qSketchRegion(id + "F18", true);
            extrude(context, id + "F20", {"entities" : qUnion([Q0]), "operationType" : NewBodyOperationType.ADD, "oppositeDirection" : true, "depth" : 5 * mm});
        }
        {
            var Q0;
            Q0=makeQuery(id+"F20.boolean.opBoolean","INTERSECT",EDGE,{"derivedFrom":[makeQuery(id+"F2.opFillet","BLEND_FACE",FACE,{"disambiguationData":[OSD([sQuery(id+"F0.wireOp",EDGE,"E0")])]}),makeQuery(id+"F20.opExtrude","SWEPT_FACE",FACE,{"disambiguationData":[OSD([sQuery(id+"F18.wireOp",EDGE,"E11")])]})]});
            var Q1;
            Q1=makeQuery(id+"F20.boolean.opBoolean","INTERSECT",EDGE,{"disambiguationData":[OD(1.0)],"derivedFrom":[makeQuery(id+"F2.opFillet","BLEND_FACE",FACE,{"disambiguationData":[OSD([sQuery(id+"F0.wireOp",EDGE,"E0")])]}),makeQuery(id+"F20.opExtrude","SWEPT_FACE",FACE,{"disambiguationData":[OSD([sQuery(id+"F18.wireOp",EDGE,"E10")])]})]});
            var Q2;
            Q2=makeQuery(id+"F20.boolean.opBoolean","INTERSECT",EDGE,{"disambiguationData":[OD(0.0)],"derivedFrom":[makeQuery(id+"F2.opFillet","BLEND_FACE",FACE,{"disambiguationData":[OSD([sQuery(id+"F0.wireOp",EDGE,"E0")])]}),makeQuery(id+"F20.opExtrude","SWEPT_FACE",FACE,{"disambiguationData":[OSD([sQuery(id+"F18.wireOp",EDGE,"E10")])]})]});
            var Q3;
            Q3=makeQuery(id+"F20.boolean.opBoolean","INTERSECT",EDGE,{"derivedFrom":[makeQuery(id+"F6.opFillet","BLEND_FACE",FACE,{"disambiguationData":[OSD([sQuery(id+"F0.wireOp",EDGE,"E0"),sQuery(id+"F3.wireOp",EDGE,"E1")])]}),makeQuery(id+"F20.opExtrude","SWEPT_FACE",FACE,{"disambiguationData":[OSD([sQuery(id+"F18.wireOp",EDGE,"E11")])]})]});
            var Q4;
            Q4=makeQuery(id+"F20.boolean.opBoolean","INTERSECT",EDGE,{"derivedFrom":[makeQuery(id+"F2.opFillet","BLEND_FACE",FACE,{"disambiguationData":[OSD([sQuery(id+"F0.wireOp",EDGE,"E0")])]}),makeQuery(id+"F20.opExtrude","SWEPT_FACE",FACE,{"disambiguationData":[OSD([sQuery(id+"F18.wireOp",EDGE,"E9")])]})]});
            var Q5;
            Q5=makeQuery(id+"F20.boolean.opBoolean","INTERSECT",EDGE,{"disambiguationData":[OD(1.0)],"derivedFrom":[makeQuery(id+"F2.opFillet","BLEND_FACE",FACE,{"disambiguationData":[OSD([sQuery(id+"F0.wireOp",EDGE,"E0")])]}),makeQuery(id+"F20.opExtrude","SWEPT_FACE",FACE,{"disambiguationData":[OSD([sQuery(id+"F18.wireOp",EDGE,"E8")])]})]});
            var Q6;
            Q6=makeQuery(id+"F20.boolean.opBoolean","INTERSECT",EDGE,{"derivedFrom":[makeQuery(id+"F6.opFillet","BLEND_FACE",FACE,{"disambiguationData":[OSD([sQuery(id+"F0.wireOp",EDGE,"E0"),sQuery(id+"F3.wireOp",EDGE,"E1")])]}),makeQuery(id+"F20.opExtrude","SWEPT_FACE",FACE,{"disambiguationData":[OSD([sQuery(id+"F18.wireOp",EDGE,"E9")])]})]});
            var Q7;
            Q7=makeQuery(id+"F20.boolean.opBoolean","INTERSECT",EDGE,{"disambiguationData":[OD(0.0)],"derivedFrom":[makeQuery(id+"F2.opFillet","BLEND_FACE",FACE,{"disambiguationData":[OSD([sQuery(id+"F0.wireOp",EDGE,"E0")])]}),makeQuery(id+"F20.opExtrude","SWEPT_FACE",FACE,{"disambiguationData":[OSD([sQuery(id+"F18.wireOp",EDGE,"E8")])]})]});
            fillet(context, id + "F21", {"entities" : qUnion([Q0, Q1, Q2, Q3, Q4, Q5, Q6, Q7]), "radius" : 5 * mm, "tangentPropagation" : true, "allowEdgeOverflow" : false});
        }
        {
            var Q0;
            Q0=makeQuery(id+"F19.boolean.opBoolean","INTERSECT",EDGE,{"disambiguationData":[OD(0.0)],"derivedFrom":[makeQuery(id+"F2.opFillet","BLEND_FACE",FACE,{"disambiguationData":[OSD([sQuery(id+"F0.wireOp",EDGE,"E0")])]}),makeQuery(id+"F19.opExtrude","CAP_FACE",FACE,{"disambiguationData":[OSD([sQuery(id+"F18.wireOp",EDGE,"E10"),sQuery(id+"F18.wireOp",EDGE,"E11")])],"isStart":false})]});
            var Q1;
            Q1=makeQuery(id+"F19.boolean.opBoolean","INTERSECT",EDGE,{"derivedFrom":[makeQuery(id+"F6.opFillet","BLEND_FACE",FACE,{"disambiguationData":[OSD([sQuery(id+"F0.wireOp",EDGE,"E0"),sQuery(id+"F3.wireOp",EDGE,"E1")])]}),makeQuery(id+"F19.opExtrude","CAP_FACE",FACE,{"disambiguationData":[OSD([sQuery(id+"F18.wireOp",EDGE,"E10"),sQuery(id+"F18.wireOp",EDGE,"E11")])],"isStart":false})]});
            var Q2;
            Q2=makeQuery(id+"F20.boolean.opBoolean","INTERSECT",EDGE,{"derivedFrom":[makeQuery(id+"F6.opFillet","BLEND_FACE",FACE,{"disambiguationData":[OSD([sQuery(id+"F0.wireOp",EDGE,"E0"),sQuery(id+"F3.wireOp",EDGE,"E1")])]}),makeQuery(id+"F20.opExtrude","CAP_FACE",FACE,{"disambiguationData":[OSD([sQuery(id+"F18.wireOp",EDGE,"E10"),sQuery(id+"F18.wireOp",EDGE,"E11")])],"isStart":false})]});
            var Q3;
            Q3=makeQuery(id+"F20.boolean.opBoolean","INTERSECT",EDGE,{"disambiguationData":[OD(0.0)],"derivedFrom":[makeQuery(id+"F2.opFillet","BLEND_FACE",FACE,{"disambiguationData":[OSD([sQuery(id+"F0.wireOp",EDGE,"E0")])]}),makeQuery(id+"F20.opExtrude","CAP_FACE",FACE,{"disambiguationData":[OSD([sQuery(id+"F18.wireOp",EDGE,"E10"),sQuery(id+"F18.wireOp",EDGE,"E11")])],"isStart":false})]});
            var Q4;
            Q4=makeQuery(id+"F19.boolean.opBoolean","INTERSECT",EDGE,{"derivedFrom":[makeQuery(id+"F6.opFillet","BLEND_FACE",FACE,{"disambiguationData":[OSD([sQuery(id+"F0.wireOp",EDGE,"E0"),sQuery(id+"F3.wireOp",EDGE,"E1")])]}),makeQuery(id+"F19.opExtrude","CAP_FACE",FACE,{"disambiguationData":[OSD([sQuery(id+"F18.wireOp",EDGE,"E8"),sQuery(id+"F18.wireOp",EDGE,"E9")])],"isStart":false})]});
            var Q5;
            Q5=makeQuery(id+"F19.boolean.opBoolean","INTERSECT",EDGE,{"disambiguationData":[OD(0.0)],"derivedFrom":[makeQuery(id+"F2.opFillet","BLEND_FACE",FACE,{"disambiguationData":[OSD([sQuery(id+"F0.wireOp",EDGE,"E0")])]}),makeQuery(id+"F19.opExtrude","CAP_FACE",FACE,{"disambiguationData":[OSD([sQuery(id+"F18.wireOp",EDGE,"E8"),sQuery(id+"F18.wireOp",EDGE,"E9")])],"isStart":false})]});
            var Q6;
            Q6=makeQuery(id+"F20.boolean.opBoolean","INTERSECT",EDGE,{"disambiguationData":[OD(0.0)],"derivedFrom":[makeQuery(id+"F2.opFillet","BLEND_FACE",FACE,{"disambiguationData":[OSD([sQuery(id+"F0.wireOp",EDGE,"E0")])]}),makeQuery(id+"F20.opExtrude","CAP_FACE",FACE,{"disambiguationData":[OSD([sQuery(id+"F18.wireOp",EDGE,"E8"),sQuery(id+"F18.wireOp",EDGE,"E9")])],"isStart":false})]});
            var Q7;
            Q7=makeQuery(id+"F20.boolean.opBoolean","INTERSECT",EDGE,{"derivedFrom":[makeQuery(id+"F6.opFillet","BLEND_FACE",FACE,{"disambiguationData":[OSD([sQuery(id+"F0.wireOp",EDGE,"E0"),sQuery(id+"F3.wireOp",EDGE,"E1")])]}),makeQuery(id+"F20.opExtrude","CAP_FACE",FACE,{"disambiguationData":[OSD([sQuery(id+"F18.wireOp",EDGE,"E8"),sQuery(id+"F18.wireOp",EDGE,"E9")])],"isStart":false})]});
            fillet(context, id + "F22", {"entities" : qUnion([Q0, Q1, Q2, Q3, Q4, Q5, Q6, Q7]), "radius" : 5 * mm, "tangentPropagation" : true, "allowEdgeOverflow" : false});
        }
        {
            var Q0;
            Q0=makeQuery(id+"F19.opExtrude","CAP_EDGE",EDGE,{"disambiguationData":[OSD([sQuery(id+"F18.wireOp",EDGE,"E11")])],"isStart":false});
            var Q1;
            Q1=makeQuery(id+"F20.opExtrude","CAP_EDGE",EDGE,{"disambiguationData":[OSD([sQuery(id+"F18.wireOp",EDGE,"E11")])],"isStart":false});
            var Q2;
            Q2=makeQuery(id+"F19.opExtrude","CAP_EDGE",EDGE,{"disambiguationData":[OSD([sQuery(id+"F18.wireOp",EDGE,"E9")])],"isStart":false});
            var Q3;
            Q3=makeQuery(id+"F20.opExtrude","CAP_EDGE",EDGE,{"disambiguationData":[OSD([sQuery(id+"F18.wireOp",EDGE,"E9")])],"isStart":false});
            var Q4;
            Q4=makeQuery(id+"F19.opExtrude","CAP_EDGE",EDGE,{"disambiguationData":[OSD([sQuery(id+"F18.wireOp",EDGE,"E10")])],"isStart":false});
            var Q5;
            Q5=makeQuery(id+"F19.opExtrude","CAP_EDGE",EDGE,{"disambiguationData":[OSD([sQuery(id+"F18.wireOp",EDGE,"E8")])],"isStart":false});
            var Q6;
            Q6=makeQuery(id+"F20.opExtrude","CAP_EDGE",EDGE,{"disambiguationData":[OSD([sQuery(id+"F18.wireOp",EDGE,"E10")])],"isStart":false});
            var Q7;
            Q7=makeQuery(id+"F20.opExtrude","CAP_EDGE",EDGE,{"disambiguationData":[OSD([sQuery(id+"F18.wireOp",EDGE,"E8")])],"isStart":false});
            fillet(context, id + "F23", {"entities" : qUnion([Q0, Q1, Q2, Q3, Q4, Q5, Q6, Q7]), "radius" : 2.5 * mm, "tangentPropagation" : true, "allowEdgeOverflow" : false});
        }
    });
